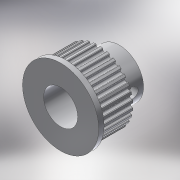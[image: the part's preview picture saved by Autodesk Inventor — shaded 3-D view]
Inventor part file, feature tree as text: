
AUTODESK INVENTOR PART (.ipt)
format: ipt  version: 2018.2 (Build 222227000, 227)  size: 311,808 bytes
history: native  units: mm
features: extrude x6, sketch x5, pattern_circular x1
ambient origin geometry x8: Origin, YZ Plane, XZ Plane, XY Plane, X Axis, Y Axis, Z Axis, Center Point
bodies: Solid1 (feature_tree)
feature tree (12):
  extrude  "Extrusion1"  Depth=0.5mm
  extrude  "Extrusion2"  Depth=7.0mm TaperAngle=0.0deg
  pattern_circular  "Circular Pattern1"  [2 undecoded]
  extrude  "Extrusion3"  Depth=1.0mm TaperAngle=0.0deg
  sketch  "Sketch4"  dims[d18=9.6mm]
  extrude  "Extrusion4"  Depth=6.0mm TaperAngle=0.0deg
  extrude  "Extrusion5"  Depth=3.0mm
  extrude  "Extrusion6"  Depth=6.0mm TaperAngle=0.0deg
  sketch  "Sketch1"  dims[d8=0.0mm d9=0.5mm]
  sketch  "Sketch2"  dims[d10=0.15mm d12=7.0mm d13=0.0mm]
  sketch  "Sketch3"  dims[d15=360.0deg]
  sketch  "Sketch5"  dims[d20=0.0mm d21=2.0mm d22=1.0mm d23=0.0mm d24=6.0mm d25=0.0mm d26=3.0mm d27=6.0mm d28=0.0mm]
note: 2 required parameter values undecoded (feature->parameter linkage not recoverable at this tier; creation-order binding heuristic only, values carry confidence <= 0.55)
